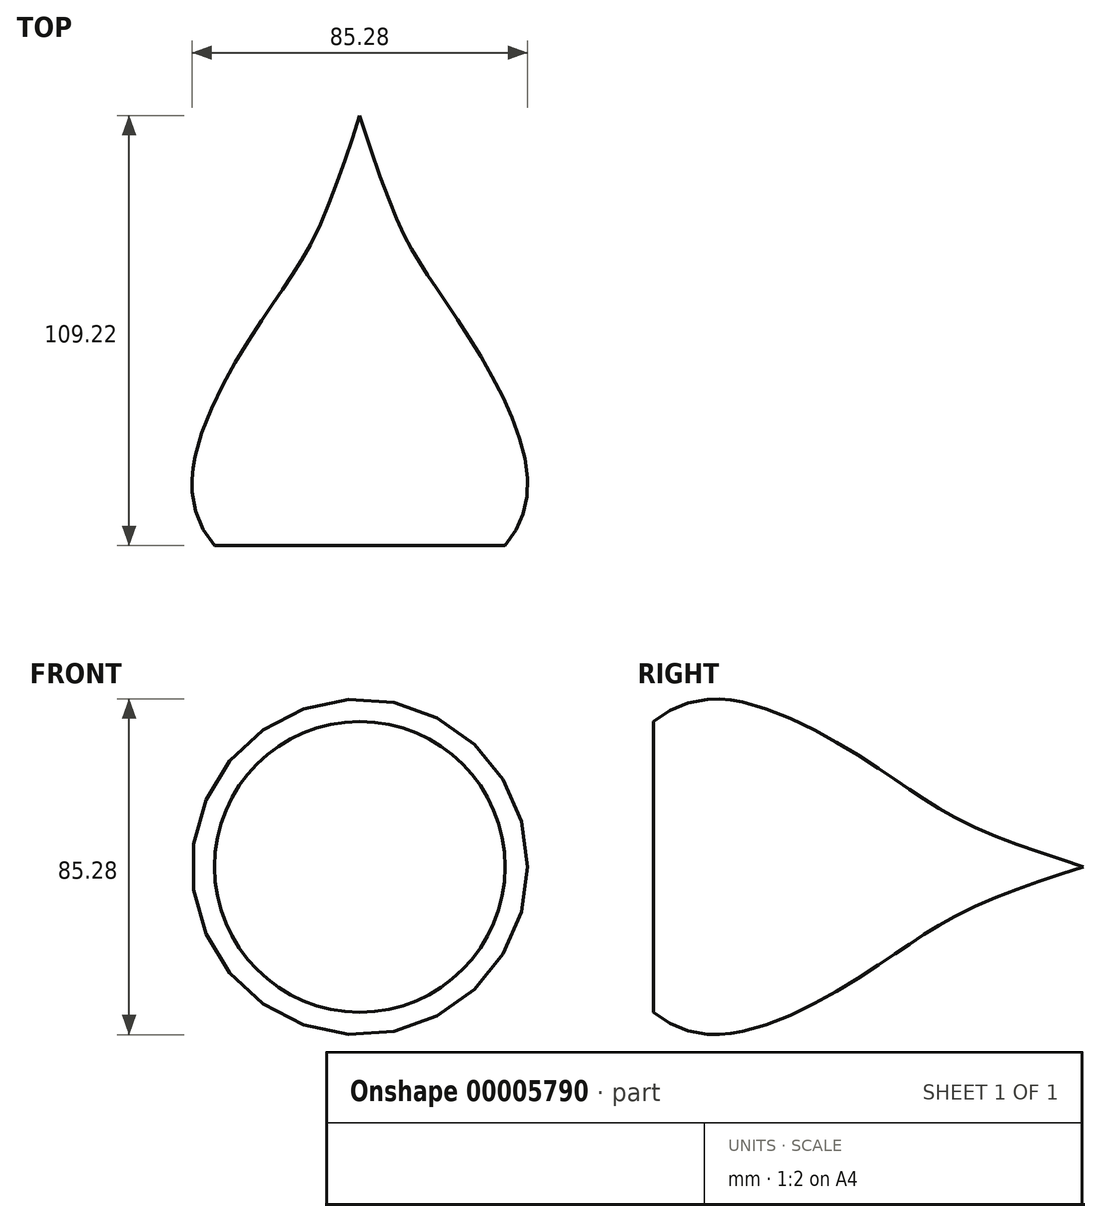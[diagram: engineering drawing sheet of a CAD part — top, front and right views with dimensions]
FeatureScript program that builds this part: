
annotation { "Feature Type Name" : "Feature", "Feature Type Description" : "" }
export const myFeature = defineFeature(function(context is Context, id is Id, definition is map)
    precondition{}
    {
        {
            var Q0;
            Q0=qCreatedBy(makeId("Top.planeOp"),FACE);
            var sketch = newSketch(context, id + "F0", { "sketchPlane" : qUnion([Q0])});
            skLineSegment(sketch, "E0", {"start": v(0, 0) * mm, "end": v(0, 127) * mm});
            skFitSpline(sketch, "E1", {"points": [v(0, 127) * mm, v(20.73, 81.25) * mm, v(42.63, 33.9) * mm, v(0, 0) * mm], "startDerivative": vector(86.22, -268.06) * mm, "endDerivative": vector(-262.22, -60.08) * mm});
            skSolve(sketch);
        }
        {
            var Q0;
            Q0 = qSketchRegion(id + "F0", true);
            var Q1;
            Q1=sQuery(id+"F0.wireOp",EDGE,"E0");
            revolve(context, id + "F1", {"entities" : qUnion([Q0]), "axis" : qUnion([Q1]), "revolveType" : RevolveType.FULL});
        }
        {
            var Q0;
            Q0=qCreatedBy(makeId("Front.planeOp"),FACE);
            var sketch = newSketch(context, id + "F2", { "sketchPlane" : qUnion([Q0])});
            skCircle(sketch, "E2", {"center": v(0, 0) * mm, "radius": 42.64 * mm});
            skSolve(sketch);
        }
        {
            var Q0;
            Q0=makeQuery(id+"F2.imprint","IMPRINT",FACE,{"disambiguationData":[TD([[makeQuery(id+"F2.imprint","IMPRINT",EDGE,{"derivedFrom":sQuery(id+"F2.wireOp",EDGE,"E2")}),1.0]])]});
            extrude(context, id + "F3", {"entities" : qUnion([Q0]), "oppositeDirection" : true, "depth" : 17.78 * mm});
        }
        {
            var Q0;
            Q0=makeQuery(id+"F3.opExtrude","SWEPT_BODY",BODY,{"disambiguationData":[OSD([sQuery(id+"F2.wireOp",EDGE,"E2")])]});
            var Q1;
            Q1=makeQuery(id+"F1.opRevolve","SWEPT_BODY",BODY,{"disambiguationData":[OSD([sQuery(id+"F0.wireOp",EDGE,"E0"),sQuery(id+"F0.wireOp",EDGE,"E1")])]});
            booleanBodies(context, id + "F4", {"operationType" : BooleanOperationType.SUBTRACTION, "tools" : qUnion([Q0]), "targets" : qUnion([Q1])});
        }
    });
